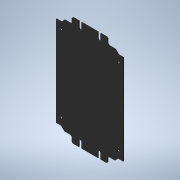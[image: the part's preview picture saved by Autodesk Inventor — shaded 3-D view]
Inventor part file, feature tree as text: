
AUTODESK INVENTOR PART (.ipt)
format: ipt  version: 2021 (Build 250183000, 183)  size: 161,792 bytes
history: native  units: mm
features: other x7, extrude x1, sketch x1
ambient origin geometry x8: Origin, YZ Plane, XZ Plane, XY Plane, X Axis, Y Axis, Z Axis, Center Point
bodies: Solid1 (feature_tree)
feature tree (9):
  extrude  "Extrusion1"  TaperAngle=0.0deg  [1 undecoded]
  other  "MONTAGEPLATTE_XY"
  other  "MONTAGEPLATTE_YZ"
  other  "MONTAGEPLATTE_ZX"
  other  "MONTAGEPLATTE_X"
  other  "MONTAGEPLATTE_Y"
  other  "MONTAGEPLATTE_Z"
  other  "MONTAGEPLATTE_Center"
  sketch  "Sketch_7"  dims[d0=2.0mm d1=0.0mm d2=0.0mm]
note: 1 required parameter value undecoded (feature->parameter linkage not recoverable at this tier; creation-order binding heuristic only, values carry confidence <= 0.55)
